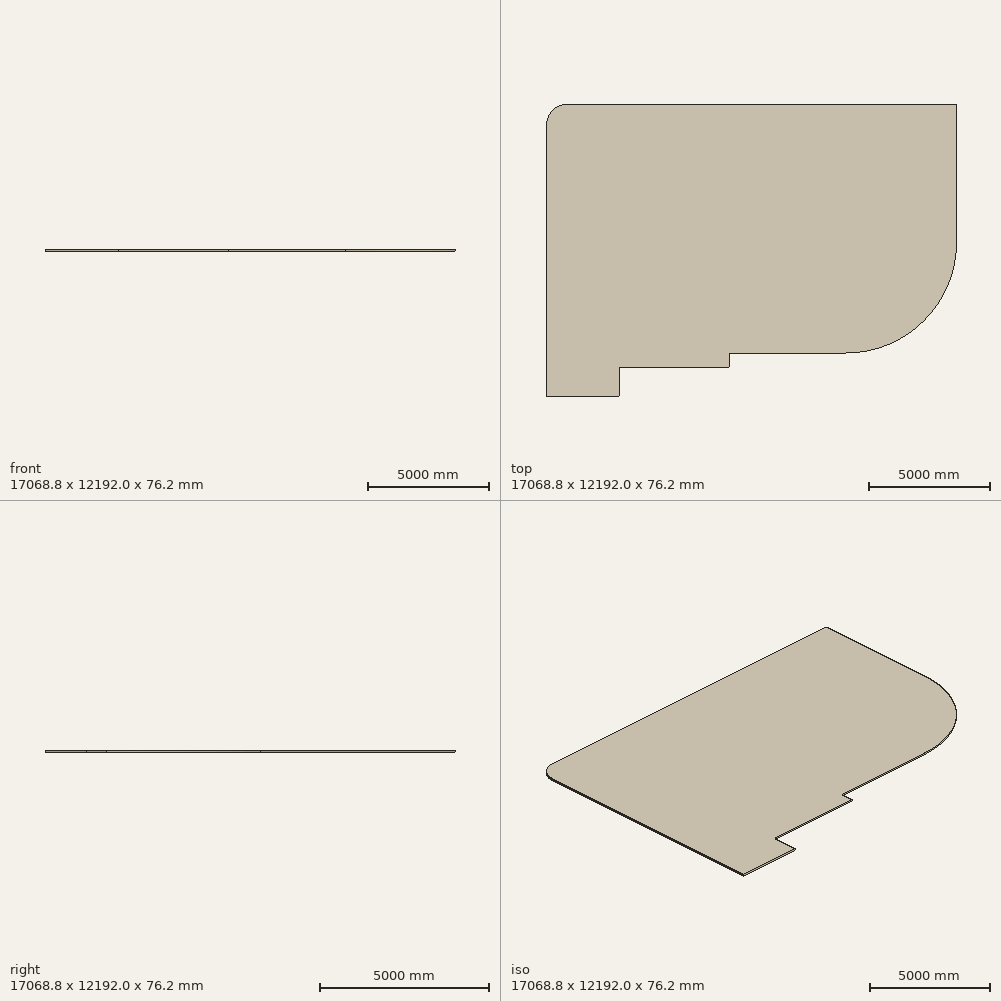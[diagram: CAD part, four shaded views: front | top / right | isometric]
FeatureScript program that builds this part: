
annotation { "Feature Type Name" : "Feature", "Feature Type Description" : "" }
export const myFeature = defineFeature(function(context is Context, id is Id, definition is map)
    precondition{}
    {
        {
            var Q0;
            Q0=qCreatedBy(makeId("Top.planeOp"),FACE);
            var sketch = newSketch(context, id + "F0", { "sketchPlane" : qUnion([Q0])});
            skLineSegment(sketch, "E0", {"start": v(-11430, 9144) * mm, "end": v(11430, 9144) * mm});
            skLineSegment(sketch, "E1", {"start": v(11430, 9144) * mm, "end": v(11430, 0) * mm});
            skLineSegment(sketch, "E2", {"start": v(-11430, 9144) * mm, "end": v(-11430, 0) * mm});
            skSolve(sketch);
        }
        {
            var Q0;
            Q0=qCreatedBy(makeId("Top.planeOp"),FACE);
            var sketch = newSketch(context, id + "F1", { "sketchPlane" : qUnion([Q0])});
            skLineSegment(sketch, "E3", {"start": v(6858, 7848.6) * mm, "end": v(-9296.4, 7848.6) * mm});
            skLineSegment(sketch, "E4", {"start": v(-10210.8, 6934.2) * mm, "end": v(-10210.8, -4343.4) * mm});
            skPoint(sketch, "E5.visualSharp", {"position": v(-10210.8, 7848.6) * mm});
            skArc(sketch, "E5.filletArc", {"start": v(-9296.4, 7848.6) * mm, "mid": v(-9942.98, 7580.78) * mm, "end": v(-10210.8, 6934.2) * mm});
            skLineSegment(sketch, "E6", {"start": v(6858, 7848.6) * mm, "end": v(6858, 2057.4) * mm});
            skLineSegment(sketch, "E7", {"start": v(2286, -2514.6) * mm, "end": v(-2590.8, -2514.6) * mm});
            skPoint(sketch, "E8.visualSharp", {"position": v(6858, -2514.6) * mm});
            skArc(sketch, "E8.filletArc", {"start": v(2286, -2514.6) * mm, "mid": v(5518.9, -1175.5) * mm, "end": v(6858, 2057.4) * mm});
            skLineSegment(sketch, "E9", {"start": v(-2590.8, -2514.6) * mm, "end": v(-2590.8, -3124.2) * mm});
            skLineSegment(sketch, "E10", {"start": v(-2590.8, -3124.2) * mm, "end": v(-7162.8, -3124.2) * mm});
            skLineSegment(sketch, "E11", {"start": v(-7162.8, -3124.2) * mm, "end": v(-7162.8, -4343.4) * mm});
            skLineSegment(sketch, "E12", {"start": v(-7162.8, -4343.4) * mm, "end": v(-10210.8, -4343.4) * mm});
            skSolve(sketch);
        }
        {
            var Q0;
            Q0=makeQuery(id+"F1.imprint","IMPRINT",FACE,{"disambiguationData":[TD([[makeQuery(id+"F1.imprint","IMPRINT",EDGE,{"derivedFrom":sQuery(id+"F1.wireOp",EDGE,"E3")}),1.0]])]});
            extrude(context, id + "F2", {"entities" : qUnion([Q0]), "depth" : 76.2 * mm, "offsetDistance" : 25.4 * mm});
        }
    });
